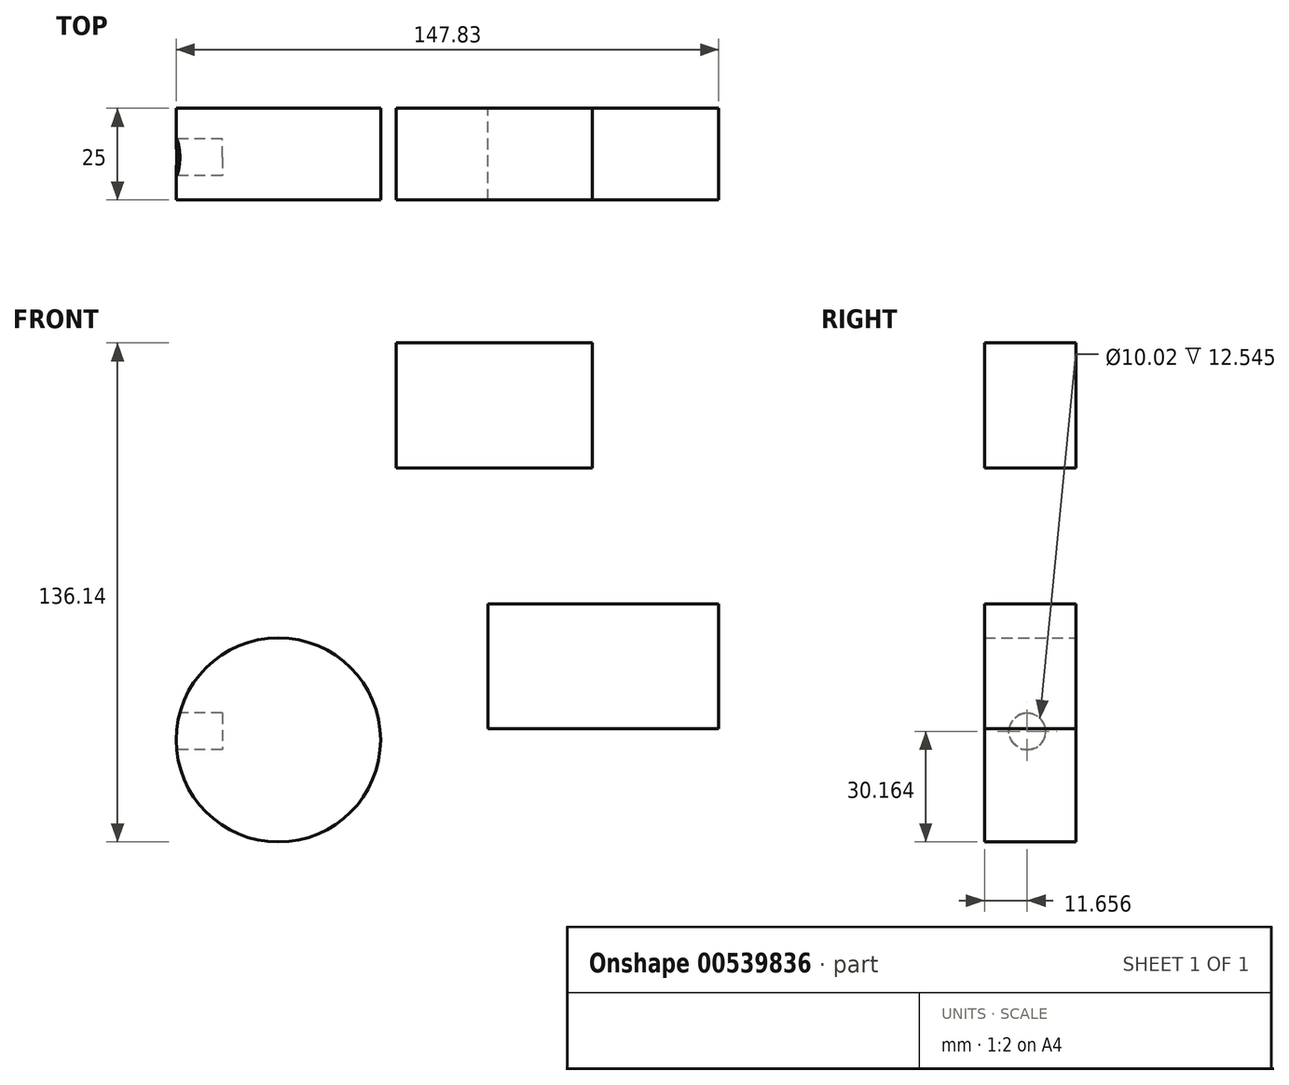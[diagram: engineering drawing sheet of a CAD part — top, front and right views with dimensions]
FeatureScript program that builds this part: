
annotation { "Feature Type Name" : "Feature", "Feature Type Description" : "" }
export const myFeature = defineFeature(function(context is Context, id is Id, definition is map)
    precondition{}
    {
        {
            var Q0;
            Q0=qCreatedBy(makeId("Front.planeOp"),FACE);
            var sketch = newSketch(context, id + "F0", { "sketchPlane" : qUnion([Q0])});
            skLineSegment(sketch, "E0.bottom", {"start": v(-111.63, 39.77) * mm, "end": v(-55.81, 39.77) * mm});
            skLineSegment(sketch, "E0.top", {"start": v(-111.63, -18.72) * mm, "end": v(-55.81, -18.72) * mm});
            skLineSegment(sketch, "E0.left", {"start": v(-111.63, 39.77) * mm, "end": v(-111.63, -18.72) * mm});
            skLineSegment(sketch, "E0.right", {"start": v(-55.81, 39.77) * mm, "end": v(-55.81, -18.72) * mm});
            skLineSegment(sketch, "E1.bottom", {"start": v(11.36, -21.39) * mm, "end": v(74.2, -21.39) * mm});
            skLineSegment(sketch, "E1.top", {"start": v(11.36, -55.48) * mm, "end": v(74.2, -55.48) * mm});
            skLineSegment(sketch, "E1.left", {"start": v(11.36, -21.39) * mm, "end": v(11.36, -55.48) * mm});
            skLineSegment(sketch, "E1.right", {"start": v(74.2, -21.39) * mm, "end": v(74.2, -55.48) * mm});
            skLineSegment(sketch, "E2.bottom", {"start": v(-13.7, 49.8) * mm, "end": v(39.77, 49.8) * mm});
            skLineSegment(sketch, "E2.top", {"start": v(-13.7, 15.7) * mm, "end": v(39.77, 15.7) * mm});
            skLineSegment(sketch, "E2.left", {"start": v(-13.7, 49.8) * mm, "end": v(-13.7, 15.7) * mm});
            skLineSegment(sketch, "E2.right", {"start": v(39.77, 49.8) * mm, "end": v(39.77, 15.7) * mm});
            skSolve(sketch);
        }
        {
            var Q0;
            Q0 = qSketchRegion(id + "F0", true);
            extrude(context, id + "F1", {"entities" : qUnion([Q0]), "depth" : 25 * mm, "offsetDistance" : 25 * mm});
        }
        {
            var Q0;
            Q0=qCreatedBy(makeId("Front.planeOp"),FACE);
            var sketch = newSketch(context, id + "F2", { "sketchPlane" : qUnion([Q0])});
            skCircle(sketch, "E3", {"center": v(109.29, 38.77) * mm, "radius": 19.54 * mm});
            skCircle(sketch, "E4", {"center": v(-45.79, -58.49) * mm, "radius": 27.86 * mm});
            skSolve(sketch);
        }
        {
            var Q0;
            Q0 = qSketchRegion(id + "F2", true);
            extrude(context, id + "F3", {"entities" : qUnion([Q0]), "depth" : 25 * mm, "offsetDistance" : 25 * mm});
        }
        {
            var Q0;
            Q0=makeQuery(id+"F1.opExtrude","SWEPT_BODY",BODY,{"disambiguationData":[OSD([sQuery(id+"F0.wireOp",EDGE,"E0.bottom"),sQuery(id+"F0.wireOp",EDGE,"E0.top"),sQuery(id+"F0.wireOp",EDGE,"E0.left"),sQuery(id+"F0.wireOp",EDGE,"E0.right")])]});
            var Q1;
            Q1=makeQuery(id+"F3.opExtrude","SWEPT_BODY",BODY,{"disambiguationData":[OSD([sQuery(id+"F2.wireOp",EDGE,"E3")])]});
            deleteBodies(context, id + "F4", {"entities" : qUnion([Q0, Q1])});
        }
        {
            var Q0;
            Q0=qCreatedBy(makeId("Right.planeOp"),FACE);
            cPlane(context, id + "F5", {"entities" : qUnion([Q0]), "cplaneType" : CPlaneType.OFFSET, "offset" : 100.4 * mm, "oppositeDirection" : true, "width" : 150 * mm, "height" : 150 * mm});
        }
        {
            var Q0;
            Q0=qCreatedBy(id+"F5.planeOp",FACE);
            var sketch = newSketch(context, id + "F6", { "sketchPlane" : qUnion([Q0])});
            skCircle(sketch, "E5", {"center": v(-13.34, -56.18) * mm, "radius": 5 * mm});
            skSolve(sketch);
        }
        {
            var Q0;
            Q0 = qSketchRegion(id + "F6", true);
            extrude(context, id + "F7", {"entities" : qUnion([Q0]), "operationType" : NewBodyOperationType.REMOVE, "depth" : 39.3 * mm, "offsetDistance" : 25 * mm});
        }
    });
